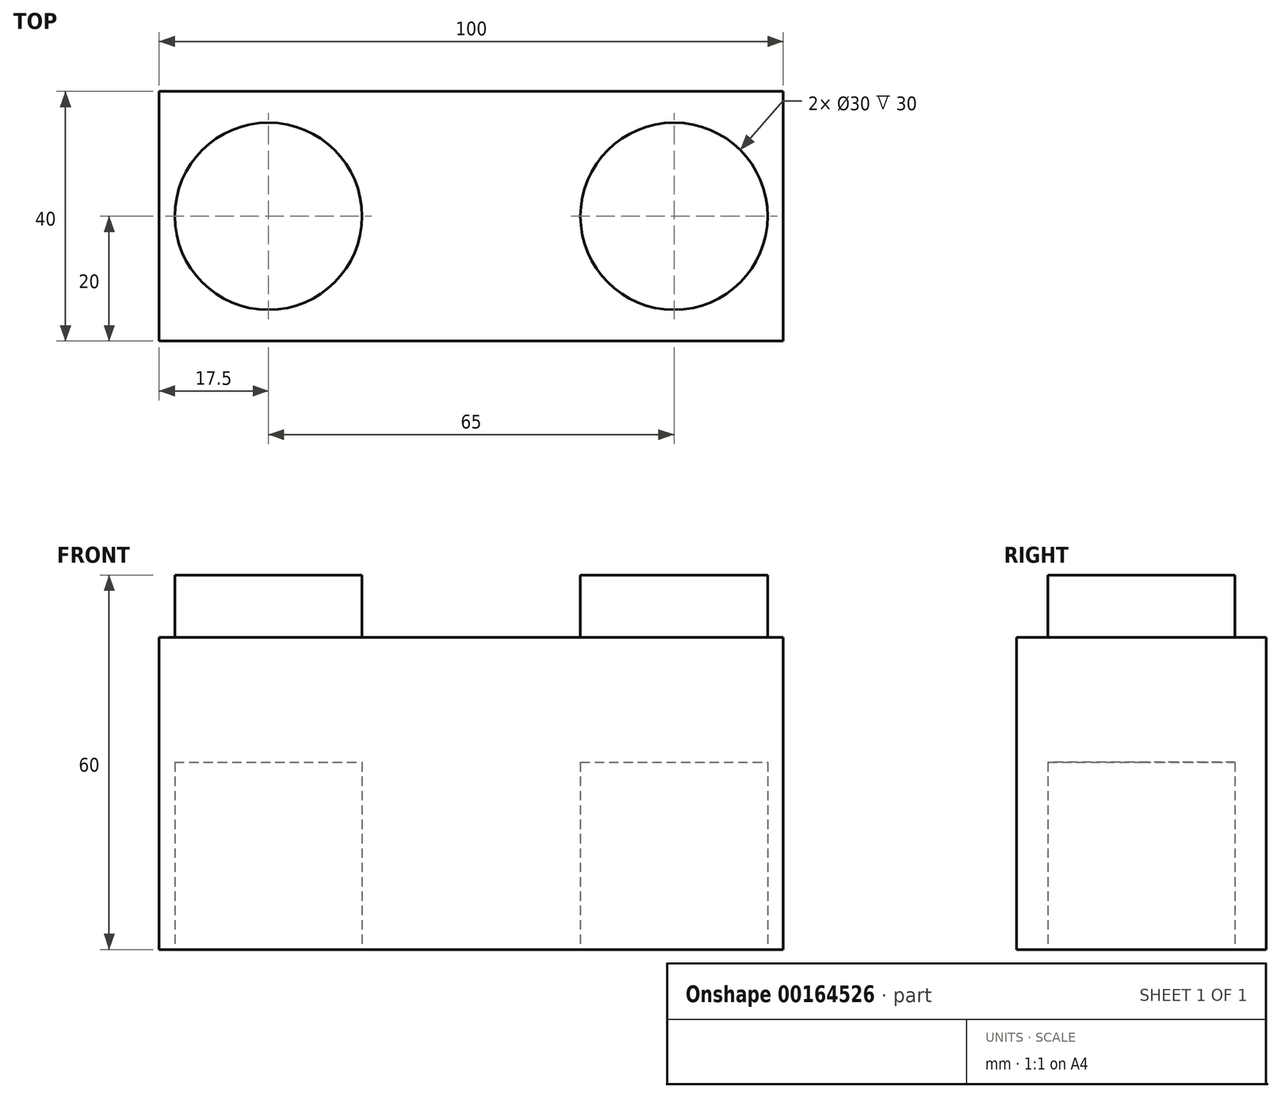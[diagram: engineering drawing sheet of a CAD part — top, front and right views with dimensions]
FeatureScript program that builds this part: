
annotation { "Feature Type Name" : "Feature", "Feature Type Description" : "" }
export const myFeature = defineFeature(function(context is Context, id is Id, definition is map)
    precondition{}
    {
        {
            var Q0;
            Q0=qCreatedBy(makeId("Front.planeOp"),FACE);
            var sketch = newSketch(context, id + "F0", { "sketchPlane" : qUnion([Q0])});
            skLineSegment(sketch, "E0.bottom", {"start": v(50, 25) * mm, "end": v(-50, 25) * mm});
            skLineSegment(sketch, "E0.top", {"start": v(50, -25) * mm, "end": v(-50, -25) * mm});
            skLineSegment(sketch, "E0.left", {"start": v(50, 25) * mm, "end": v(50, -25) * mm});
            skLineSegment(sketch, "E0.right", {"start": v(-50, 25) * mm, "end": v(-50, -25) * mm});
            skPoint(sketch, "E0.middle", {"position": v(0, 0) * mm});
            skSolve(sketch);
        }
        {
            var Q0;
            Q0 = qSketchRegion(id + "F0", true);
            extrude(context, id + "F1", {"entities" : qUnion([Q0]), "depth" : 40 * mm});
        }
        {
            var Q0;
            Q0=makeQuery(id+"F1.opExtrude","SWEPT_FACE",FACE,{"disambiguationData":[OSD([sQuery(id+"F0.wireOp",EDGE,"E0.bottom")])]});
            var sketch = newSketch(context, id + "F2", { "sketchPlane" : qUnion([Q0])});
            skCircle(sketch, "E1", {"center": v(-32.5, -20) * mm, "radius": 15 * mm});
            skPoint(sketch, "E1.centerSnap0", {"position": v(-50, -20) * mm});
            skPoint(sketch, "E1.centerSnap1", {"position": v(-32.5, -40) * mm});
            skCircle(sketch, "E2", {"center": v(32.5, -20) * mm, "radius": 15 * mm});
            skPoint(sketch, "E2.centerSnap0", {"position": v(50, -20) * mm});
            skPoint(sketch, "E2.centerSnap1", {"position": v(32.5, -40) * mm});
            skPoint(sketch, "E3.orphan", {"position": v(-50, -40) * mm});
            skPoint(sketch, "E4.end.orphan", {"position": v(-15, -40) * mm});
            skPoint(sketch, "E5.orphan", {"position": v(15, -40) * mm});
            skPoint(sketch, "E6.start.orphan", {"position": v(50, -40) * mm});
            skSolve(sketch);
        }
        {
            var Q0;
            Q0 = qSketchRegion(id + "F2", true);
            extrude(context, id + "F3", {"entities" : qUnion([Q0]), "operationType" : NewBodyOperationType.ADD, "depth" : 10 * mm});
        }
        {
            var Q0;
            Q0=makeQuery(id+"F1.opExtrude","SWEPT_FACE",FACE,{"disambiguationData":[OSD([sQuery(id+"F0.wireOp",EDGE,"E0.top")])]});
            var sketch = newSketch(context, id + "F4", { "sketchPlane" : qUnion([Q0])});
            skLineSegment(sketch, "E7", {"start": v(-50, 0) * mm, "end": v(-15, 0) * mm});
            skLineSegment(sketch, "E8", {"start": v(50, 0) * mm, "end": v(15, 0) * mm});
            skCircle(sketch, "E9", {"center": v(-32.5, 20) * mm, "radius": 15 * mm});
            skPoint(sketch, "E9.centerSnap0", {"position": v(-32.5, 0) * mm});
            skPoint(sketch, "E9.centerSnap1", {"position": v(-50, 20) * mm});
            skCircle(sketch, "E10", {"center": v(32.5, 20) * mm, "radius": 15 * mm});
            skPoint(sketch, "E10.centerSnap0", {"position": v(50, 20) * mm});
            skPoint(sketch, "E10.centerSnap1", {"position": v(32.5, 0) * mm});
            skSolve(sketch);
        }
        {
            var Q0;
            Q0 = qSketchRegion(id + "F4", true);
            extrude(context, id + "F5", {"entities" : qUnion([Q0]), "operationType" : NewBodyOperationType.REMOVE, "oppositeDirection" : true, "depth" : 30 * mm});
        }
    });
